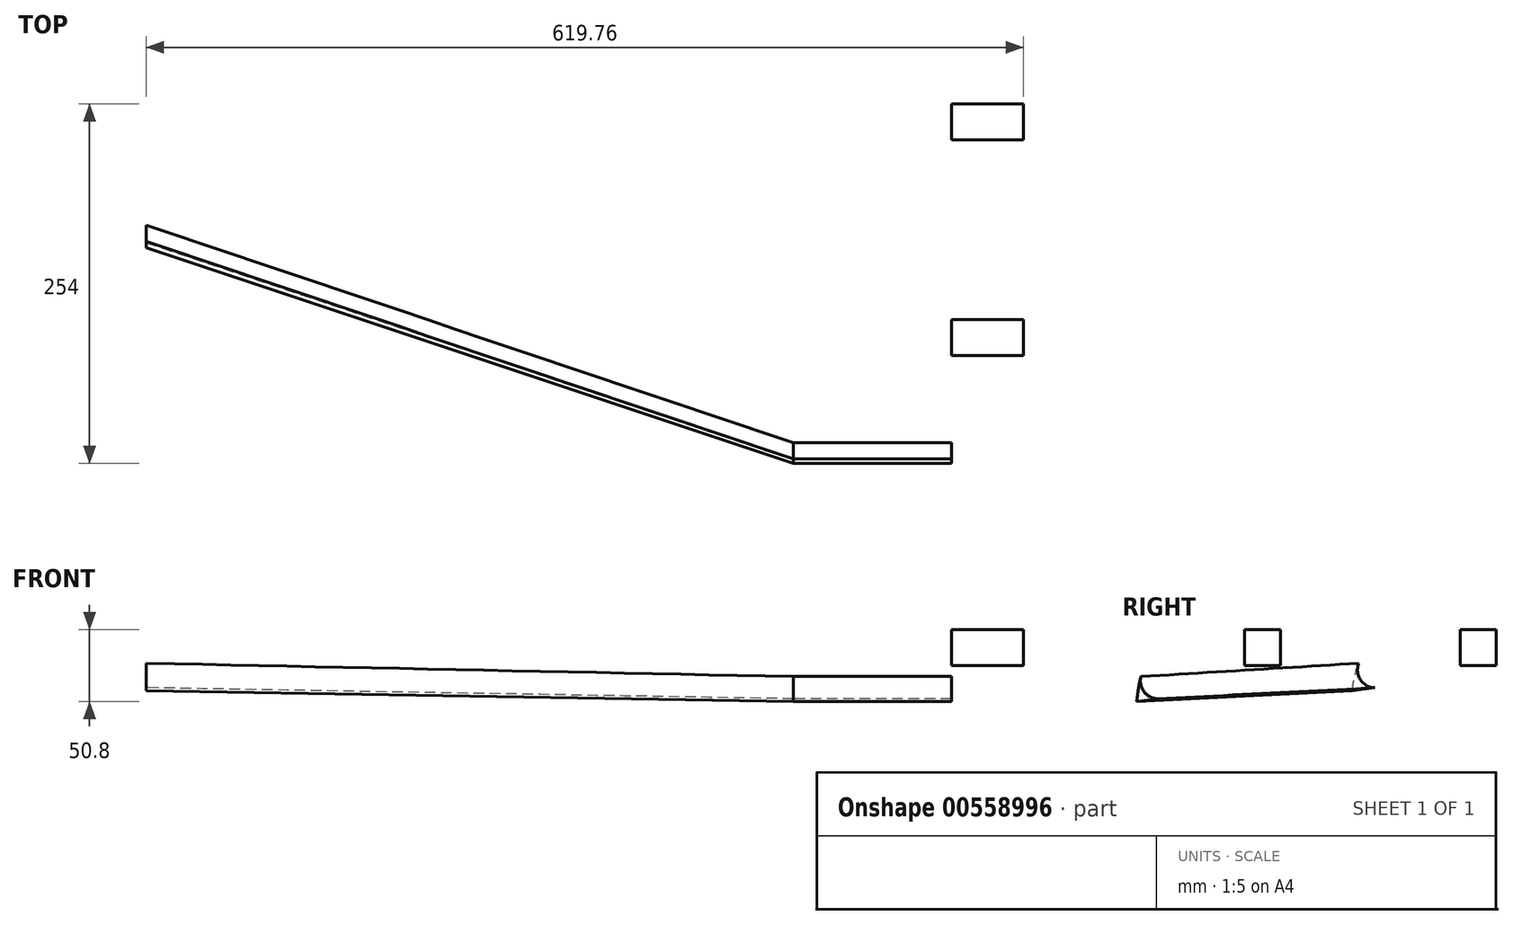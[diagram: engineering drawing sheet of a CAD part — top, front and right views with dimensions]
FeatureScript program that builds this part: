
annotation { "Feature Type Name" : "Feature", "Feature Type Description" : "" }
export const myFeature = defineFeature(function(context is Context, id is Id, definition is map)
    precondition{}
    {
        {
            var Q0;
            Q0=qCreatedBy(makeId("Right.planeOp"),FACE);
            var sketch = newSketch(context, id + "F0", { "sketchPlane" : qUnion([Q0])});
            skPoint(sketch, "E0", {"position": v(0, 0) * mm});
            skPoint(sketch, "E1", {"position": v(76.2, 76.2) * mm});
            skPoint(sketch, "E2", {"position": v(381, 38.1) * mm});
            skPoint(sketch, "E3", {"position": v(533.4, 0) * mm});
            skPoint(sketch, "E4", {"position": v(381, 6.35) * mm});
            skFitSpline(sketch, "E5", {"points": [v(0, 0) * mm, v(76.2, 76.2) * mm, v(381, 38.1) * mm, v(533.4, 0) * mm, v(381, 6.35) * mm], "startDerivative": vector(81.46, 775.02) * mm, "endDerivative": vector(-965.3, 69.79) * mm});
            skLineSegment(sketch, "E6", {"start": v(5.34, 50.8) * mm, "end": v(0, 0) * mm});
            skLineSegment(sketch, "E7", {"start": v(0, 0) * mm, "end": v(0, 58.95) * mm});
            skFitSpline(sketch, "E8", {"points": [v(381, 6.35) * mm, v(0, 0) * mm], "startDerivative": vector(-151.2, 19.05) * mm, "endDerivative": vector(-291.33, -38.1) * mm});
            skLineSegment(sketch, "E9", {"start": v(381, 6.35) * mm, "end": v(381, 26.18) * mm});
            skLineSegment(sketch, "E10", {"start": v(330.6, 12.7) * mm, "end": v(381, 6.35) * mm});
            skLineSegment(sketch, "E11", {"start": v(0, 0) * mm, "end": v(97.11, 12.7) * mm});
            skArc(sketch, "E12.filletArc", {"start": v(3.03, 17.63) * mm, "mid": v(5.76, 6.24) * mm, "end": v(16.65, 1.92) * mm});
            skSolve(sketch);
        }
        {
            var Q0;
            {var subQ0=sQuery(id+"F0.wireOp",EDGE,"E5");Q0=makeQuery(id+"F0.imprint","IMPRINT",FACE,{"disambiguationData":[TD([[makeQuery(id+"F0.imprint","IMPRINT",EDGE,{"derivedFrom":subQ0}),-1.0]])]});}
            extrude(context, id + "F1", {"entities" : qUnion([Q0]), "depth" : 111.76 * mm, "offsetDistance" : 25.4 * mm});
        }
        {
            var Q0;
            Q0=makeQuery(id+"F1.opExtrude","CAP_FACE",FACE,{"disambiguationData":[OSD([sQuery(id+"F0.wireOp",EDGE,"E5"),sQuery(id+"F0.wireOp",EDGE,"E8"),sQuery(id+"F0.wireOp",EDGE,"E12.filletArc")])],"isStart":false});
            cPlane(context, id + "F2", {"entities" : qUnion([Q0]), "cplaneType" : CPlaneType.OFFSET, "offset" : 457.2 * mm, "width" : 152.4 * mm, "height" : 152.4 * mm});
        }
        {
            var Q0;
            Q0=qCreatedBy(id+"F2.planeOp",FACE);
            var sketch = newSketch(context, id + "F3", { "sketchPlane" : qUnion([Q0])});
            skPoint(sketch, "E13", {"position": v(152.4, 7.62) * mm});
            skPoint(sketch, "E14", {"position": v(508, 7.62) * mm});
            skPoint(sketch, "E15", {"position": v(406.4, 13.17) * mm});
            skPoint(sketch, "E16", {"position": v(406.4, 33.02) * mm});
            skPoint(sketch, "E17", {"position": v(203.2, 58.42) * mm});
            skFitSpline(sketch, "E18", {"points": [v(152.4, 7.62) * mm, v(203.2, 58.42) * mm, v(406.4, 33.02) * mm, v(508, 7.62) * mm, v(406.4, 13.17) * mm], "startDerivative": vector(54.3, 516.72) * mm, "endDerivative": vector(-643.37, 57.95) * mm});
            skFitSpline(sketch, "E19", {"points": [v(406.4, 13.17) * mm, v(152.4, 7.62) * mm], "startDerivative": vector(-151.2, 19.05) * mm, "endDerivative": vector(-291.33, -38.1) * mm});
            skLineSegment(sketch, "E20", {"start": v(155.96, 41.49) * mm, "end": v(152.4, 7.62) * mm});
            skLineSegment(sketch, "E21", {"start": v(152.4, 7.62) * mm, "end": v(152.4, 36.52) * mm});
            skLineSegment(sketch, "E22", {"start": v(249.51, 20.32) * mm, "end": v(152.4, 7.62) * mm});
            skArc(sketch, "E23.filletArc", {"start": v(156.82, 27) * mm, "mid": v(158.6, 14.65) * mm, "end": v(170.08, 9.78) * mm});
            skLineSegment(sketch, "E24", {"start": v(356, 19.52) * mm, "end": v(406.4, 13.17) * mm});
            skLineSegment(sketch, "E25", {"start": v(406.4, 26.03) * mm, "end": v(406.4, 13.17) * mm});
            skSolve(sketch);
        }
        {
            var Q0;
            Q0=makeQuery(id+"F1.opExtrude","CAP_FACE",FACE,{"disambiguationData":[OSD([sQuery(id+"F0.wireOp",EDGE,"E5"),sQuery(id+"F0.wireOp",EDGE,"E8"),sQuery(id+"F0.wireOp",EDGE,"E12.filletArc")])],"isStart":false});
            var Q1;
            {var subQ0=sQuery(id+"F3.wireOp",EDGE,"E18");Q1=makeQuery(id+"F3.imprint","IMPRINT",FACE,{"disambiguationData":[TD([[makeQuery(id+"F3.imprint","IMPRINT",EDGE,{"derivedFrom":subQ0}),-1.0]])]});}
            loft(context, id + "F4", {"operationType" : NewBodyOperationType.ADD, "sheetProfilesArray" : [{ "sheetProfileEntities" : qUnion([Q0]) }, { "sheetProfileEntities" : qUnion([Q1]) }]});
        }
        {
            var Q0;
            {var subQ0=sQuery(id+"F3.wireOp",EDGE,"E18");Q0=makeQuery(id+"F4.opLoft","CAP_FACE",FACE,{"disambiguationData":[OSD([makeQuery(id+"F3.imprint","IMPRINT",FACE,{"disambiguationData":[TD([[makeQuery(id+"F3.imprint","IMPRINT",EDGE,{"derivedFrom":subQ0}),-1.0]])]})])],"isStart":true});}
            var sketch = newSketch(context, id + "F5", { "sketchPlane" : qUnion([Q0])});
            skCircle(sketch, "E26", {"center": v(200.02, 34.64) * mm, "radius": 12.7 * mm});
            skSolve(sketch);
        }
        {
            var Q0;
            Q0=makeQuery(id+"F5.imprint","IMPRINT",FACE,{"disambiguationData":[TD([[makeQuery(id+"F5.imprint","IMPRINT",EDGE,{"derivedFrom":sQuery(id+"F5.wireOp",EDGE,"E26")}),1.0]])]});
            extrude(context, id + "F6", {"entities" : qUnion([Q0]), "operationType" : NewBodyOperationType.REMOVE, "oppositeDirection" : true, "depth" : 25.4 * mm, "offsetDistance" : 25.4 * mm});
        }
        {
            var Q0;
            Q0=makeQuery(id+"F1.opExtrude","SWEPT_BODY",BODY,{"disambiguationData":[OSD([sQuery(id+"F0.wireOp",EDGE,"E5"),sQuery(id+"F0.wireOp",EDGE,"E8"),sQuery(id+"F0.wireOp",EDGE,"E12.filletArc")])]});
            var Q1;
            Q1=qCreatedBy(makeId("Right.planeOp"),FACE);
            mirror(context, id + "F7", {"operationType" : NewBodyOperationType.ADD, "entities" : qUnion([Q0]), "mirrorPlane" : qUnion([Q1])});
        }
        {
            var Q0;
            Q0=qCreatedBy(makeId("Top.planeOp"),FACE);
            var sketch = newSketch(context, id + "F8", { "sketchPlane" : qUnion([Q0])});
            skLineSegment(sketch, "E27.bottom", {"start": v(0, 0) * mm, "end": v(625.5, 0) * mm});
            skLineSegment(sketch, "E27.top", {"start": v(0, 601.77) * mm, "end": v(625.5, 601.77) * mm});
            skLineSegment(sketch, "E27.left", {"start": v(0, 0) * mm, "end": v(0, 601.77) * mm});
            skLineSegment(sketch, "E27.right", {"start": v(625.5, 0) * mm, "end": v(625.5, 601.77) * mm});
            skSolve(sketch);
        }
        {
            var Q0;
            Q0=makeQuery(id+"F8.imprint","IMPRINT",FACE,{"disambiguationData":[TD([[makeQuery(id+"F8.imprint","IMPRINT",EDGE,{"derivedFrom":sQuery(id+"F8.wireOp",EDGE,"E27.bottom")}),1.0]])]});
            extrude(context, id + "F9", {"entities" : qUnion([Q0]), "operationType" : NewBodyOperationType.REMOVE, "endBound" : BoundingType.SYMMETRIC, "depth" : 254 * mm, "offsetDistance" : 25.4 * mm});
        }
        {
            var Q0;
            Q0=makeQuery(id+"F9.boolean.opBoolean","COPY",FACE,{"derivedFrom":makeQuery(id+"F9.opExtrude","SWEPT_FACE",FACE,{"disambiguationData":[OSD([sQuery(id+"F8.wireOp",EDGE,"E27.left")])]})});
            var sketch = newSketch(context, id + "F10", { "sketchPlane" : qUnion([Q0])});
            skLineSegment(sketch, "E28.bottom", {"start": v(50.8, 25.4) * mm, "end": v(76.2, 25.4) * mm});
            skLineSegment(sketch, "E28.top", {"start": v(50.8, 50.8) * mm, "end": v(76.2, 50.8) * mm});
            skLineSegment(sketch, "E28.left", {"start": v(50.8, 25.4) * mm, "end": v(50.8, 50.8) * mm});
            skLineSegment(sketch, "E28.right", {"start": v(76.2, 25.4) * mm, "end": v(76.2, 50.8) * mm});
            skLineSegment(sketch, "E29.bottom", {"start": v(203.2, 25.4) * mm, "end": v(228.6, 25.4) * mm});
            skLineSegment(sketch, "E29.top", {"start": v(203.2, 50.8) * mm, "end": v(228.6, 50.8) * mm});
            skLineSegment(sketch, "E29.left", {"start": v(203.2, 25.4) * mm, "end": v(203.2, 50.8) * mm});
            skLineSegment(sketch, "E29.right", {"start": v(228.6, 25.4) * mm, "end": v(228.6, 50.8) * mm});
            skLineSegment(sketch, "E30.MirrorCS", {"start": v(101.6, 50.8) * mm, "end": v(76.2, 50.8) * mm});
            skLineSegment(sketch, "E31.MirrorCS", {"start": v(101.6, 25.4) * mm, "end": v(101.6, 50.8) * mm});
            skLineSegment(sketch, "E32.MirrorCS", {"start": v(101.6, 25.4) * mm, "end": v(76.2, 25.4) * mm});
            skLineSegment(sketch, "E33.MirrorCS", {"start": v(254, 25.4) * mm, "end": v(228.6, 25.4) * mm});
            skLineSegment(sketch, "E34.MirrorCS", {"start": v(254, 25.4) * mm, "end": v(254, 50.8) * mm});
            skLineSegment(sketch, "E35.MirrorCS", {"start": v(254, 50.8) * mm, "end": v(228.6, 50.8) * mm});
            skSolve(sketch);
        }
        {
            var Q0;
            Q0=makeQuery(id+"F10.imprint","IMPRINT",FACE,{"disambiguationData":[TD([[makeQuery(id+"F10.imprint","IMPRINT",EDGE,{"derivedFrom":sQuery(id+"F10.wireOp",EDGE,"E29.right")}),-1.0]])]});
            var Q1;
            Q1=makeQuery(id+"F10.imprint","IMPRINT",FACE,{"disambiguationData":[TD([[makeQuery(id+"F10.imprint","IMPRINT",EDGE,{"derivedFrom":sQuery(id+"F10.wireOp",EDGE,"E28.right")}),-1.0]])]});
            extrude(context, id + "F11", {"entities" : qUnion([Q0, Q1]), "operationType" : NewBodyOperationType.ADD, "depth" : 50.8 * mm, "offsetDistance" : 25.4 * mm});
        }
        {
            var Q0;
            Q0=qCreatedBy(makeId("Top.planeOp"),FACE);
            var sketch = newSketch(context, id + "F12", { "sketchPlane" : qUnion([Q0])});
            skLineSegment(sketch, "E36.bottom", {"start": v(-118.11, 91.93) * mm, "end": v(-334.01, 91.93) * mm});
            skLineSegment(sketch, "E36.top", {"start": v(-118.11, 117.33) * mm, "end": v(-334.01, 117.33) * mm});
            skLineSegment(sketch, "E36.left", {"start": v(-111.76, 98.28) * mm, "end": v(-111.76, 110.98) * mm});
            skLineSegment(sketch, "E36.right", {"start": v(-340.36, 98.28) * mm, "end": v(-340.36, 110.98) * mm});
            skPoint(sketch, "E37.visualSharp", {"position": v(-340.36, 91.93) * mm});
            skArc(sketch, "E37.filletArc", {"start": v(-340.36, 98.28) * mm, "mid": v(-338.5, 93.79) * mm, "end": v(-334.01, 91.93) * mm});
            skPoint(sketch, "E38.visualSharp", {"position": v(-340.36, 117.33) * mm});
            skArc(sketch, "E38.filletArc", {"start": v(-334.01, 117.33) * mm, "mid": v(-338.5, 115.47) * mm, "end": v(-340.36, 110.98) * mm});
            skPoint(sketch, "E39.visualSharp", {"position": v(-111.76, 91.93) * mm});
            skArc(sketch, "E39.filletArc", {"start": v(-118.11, 91.93) * mm, "mid": v(-113.62, 93.79) * mm, "end": v(-111.76, 98.28) * mm});
            skPoint(sketch, "E40.visualSharp", {"position": v(-111.76, 117.33) * mm});
            skArc(sketch, "E40.filletArc", {"start": v(-111.76, 110.98) * mm, "mid": v(-113.62, 115.47) * mm, "end": v(-118.11, 117.33) * mm});
            skSolve(sketch);
        }
        {
            var Q0;
            Q0=makeQuery(id+"F12.imprint","IMPRINT",FACE,{"disambiguationData":[TD([[makeQuery(id+"F12.imprint","IMPRINT",EDGE,{"derivedFrom":sQuery(id+"F12.wireOp",EDGE,"E36.bottom")}),-1.0]])]});
            extrude(context, id + "F13", {"entities" : qUnion([Q0]), "operationType" : NewBodyOperationType.REMOVE, "endBound" : BoundingType.SYMMETRIC, "oppositeDirection" : true, "depth" : 419.1 * mm, "offsetDistance" : 25.4 * mm});
        }
    });
